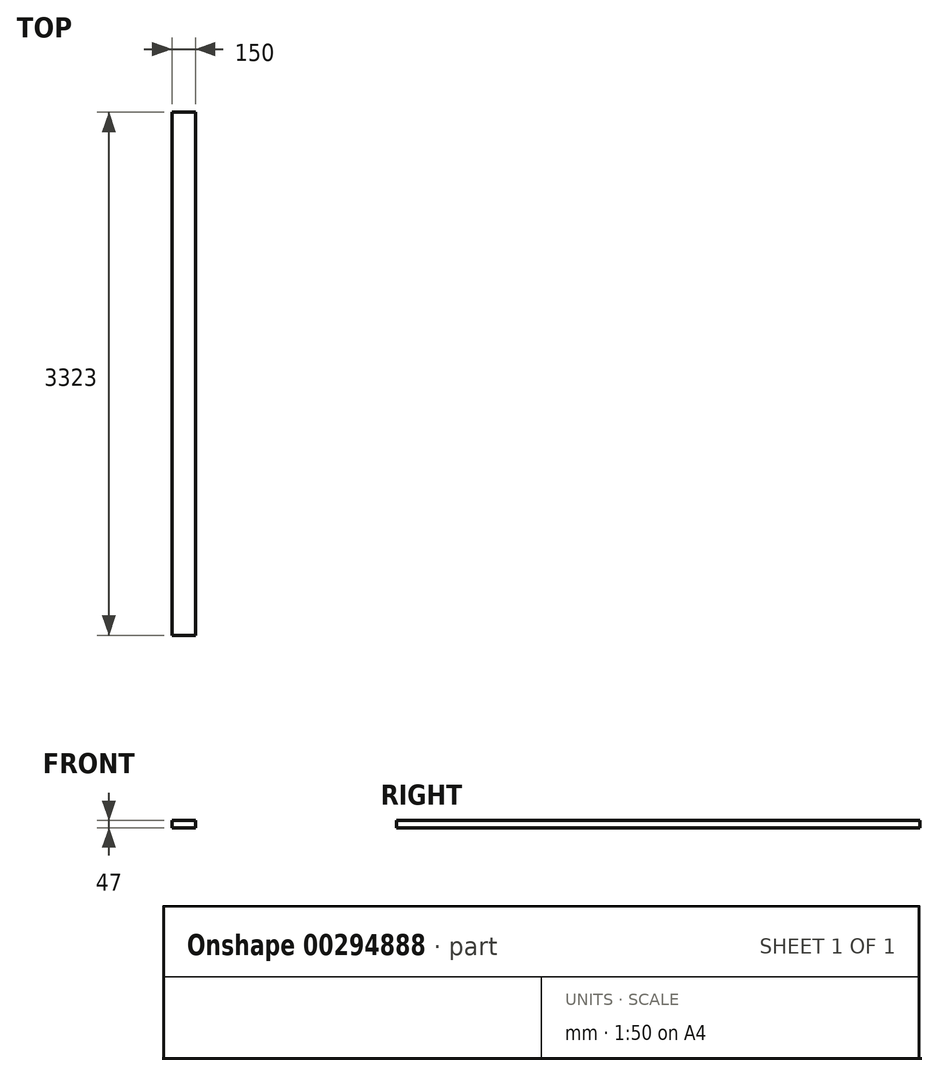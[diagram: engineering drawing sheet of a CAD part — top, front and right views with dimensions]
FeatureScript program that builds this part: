
annotation { "Feature Type Name" : "Feature", "Feature Type Description" : "" }
export const myFeature = defineFeature(function(context is Context, id is Id, definition is map)
    precondition{}
    {
        {
            var Q0;
            Q0=qCreatedBy(makeId("Front.planeOp"),FACE);
            var sketch = newSketch(context, id + "F0", { "sketchPlane" : qUnion([Q0])});
            skLineSegment(sketch, "E0.bottom", {"start": v(75, 23.5) * mm, "end": v(-75, 23.5) * mm});
            skLineSegment(sketch, "E0.top", {"start": v(75, -23.5) * mm, "end": v(-75, -23.5) * mm});
            skLineSegment(sketch, "E0.left", {"start": v(75, 23.5) * mm, "end": v(75, -23.5) * mm});
            skLineSegment(sketch, "E0.right", {"start": v(-75, 23.5) * mm, "end": v(-75, -23.5) * mm});
            skPoint(sketch, "E0.middle", {"position": v(0, 0) * mm});
            skSolve(sketch);
        }
        {
            var Q0;
            Q0 = qSketchRegion(id + "F0", true);
            extrude(context, id + "F1", {"entities" : qUnion([Q0]), "depth" : (3200 - 94 - 217 + 308 + 126) * mm});
        }
    });
